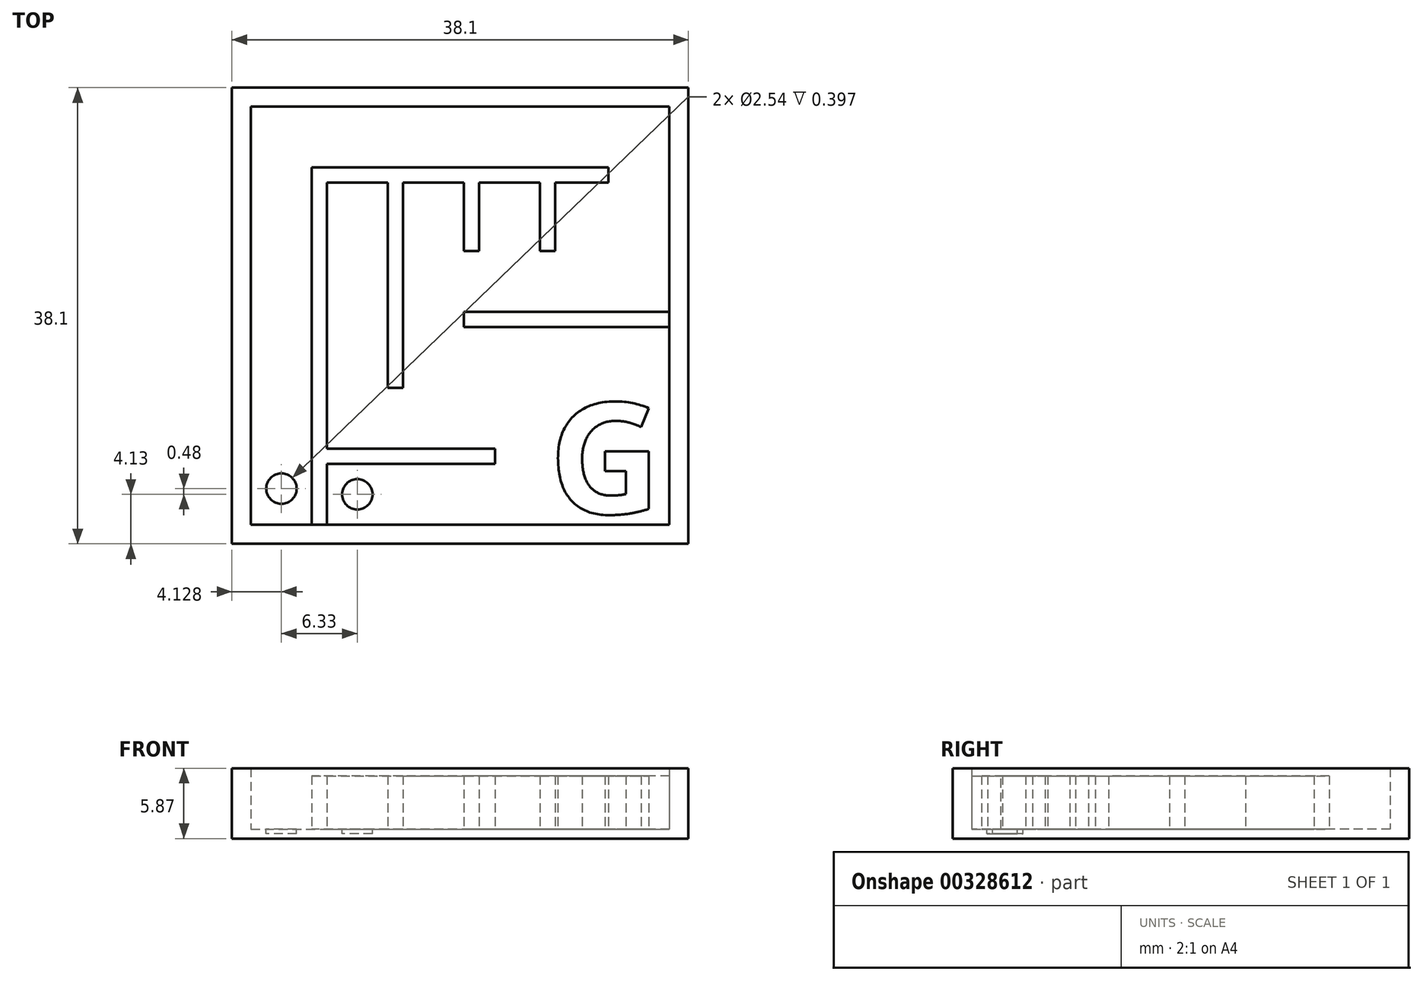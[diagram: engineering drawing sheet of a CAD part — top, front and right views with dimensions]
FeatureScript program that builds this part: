
annotation { "Feature Type Name" : "Feature", "Feature Type Description" : "" }
export const myFeature = defineFeature(function(context is Context, id is Id, definition is map)
    precondition{}
    {
        {
            var Q0;
            Q0=qCreatedBy(makeId("Top.planeOp"),FACE);
            var sketch = newSketch(context, id + "F0", { "sketchPlane" : qUnion([Q0])});
            skLineSegment(sketch, "E0.bottom", {"start": v(-19.76, 15.68) * mm, "end": v(18.34, 15.68) * mm});
            skLineSegment(sketch, "E0.top", {"start": v(-19.76, -22.42) * mm, "end": v(18.34, -22.42) * mm});
            skLineSegment(sketch, "E0.left", {"start": v(-19.76, 15.68) * mm, "end": v(-19.76, -22.42) * mm});
            skLineSegment(sketch, "E0.right", {"start": v(18.34, 15.68) * mm, "end": v(18.34, -22.42) * mm});
            skSolve(sketch);
        }
        {
            var Q0;
            Q0 = qSketchRegion(id + "F0", true);
            extrude(context, id + "F1", {"entities" : qUnion([Q0]), "depth" : 0.8 * mm});
        }
        {
            var Q0;
            Q0=makeQuery(id+"F1.opExtrude","CAP_FACE",FACE,{"disambiguationData":[OSD([sQuery(id+"F0.wireOp",EDGE,"E0.bottom"),sQuery(id+"F0.wireOp",EDGE,"E0.top"),sQuery(id+"F0.wireOp",EDGE,"E0.left"),sQuery(id+"F0.wireOp",EDGE,"E0.right")])],"isStart":false});
            var sketch = newSketch(context, id + "F2", { "sketchPlane" : qUnion([Q0])});
            skLineSegment(sketch, "E1.0", {"start": v(-18.17, 14.1) * mm, "end": v(16.75, 14.1) * mm});
            skLineSegment(sketch, "E1.1", {"start": v(-18.17, 14.1) * mm, "end": v(-18.17, -20.83) * mm});
            skLineSegment(sketch, "E1.2", {"start": v(-18.17, -20.83) * mm, "end": v(16.75, -20.83) * mm});
            skLineSegment(sketch, "E1.3", {"start": v(16.75, 14.1) * mm, "end": v(16.75, -20.83) * mm});
            skSolve(sketch);
        }
        {
            var Q0;
            Q0=makeQuery(id+"F2.imprint","IMPRINT",FACE,{"disambiguationData":[TD([[makeQuery(id+"F2.imprint","IMPRINT",EDGE,{"derivedFrom":sQuery(id+"F2.wireOp",EDGE,"E1.0")}),1.0]])]});
            extrude(context, id + "F3", {"entities" : qUnion([Q0]), "operationType" : NewBodyOperationType.ADD, "depth" : 5.08 * mm});
        }
        {
            var Q0;
            Q0=makeQuery(id+"F1.opExtrude","CAP_FACE",FACE,{"disambiguationData":[OSD([sQuery(id+"F0.wireOp",EDGE,"E0.bottom"),sQuery(id+"F0.wireOp",EDGE,"E0.top"),sQuery(id+"F0.wireOp",EDGE,"E0.left"),sQuery(id+"F0.wireOp",EDGE,"E0.right")])],"isStart":false});
            var sketch = newSketch(context, id + "F4", { "sketchPlane" : qUnion([Q0])});
            skLineSegment(sketch, "E2.bottom", {"start": v(-11.82, -20.83) * mm, "end": v(-13.1, -20.83) * mm});
            skLineSegment(sketch, "E2.top", {"start": v(-11.82, 9.02) * mm, "end": v(-13.1, 9.02) * mm});
            skLineSegment(sketch, "E2.left", {"start": v(-11.82, -20.83) * mm, "end": v(-11.82, 9.02) * mm});
            skLineSegment(sketch, "E2.right", {"start": v(-13.1, -20.83) * mm, "end": v(-13.1, 9.02) * mm});
            skLineSegment(sketch, "E3.bottom", {"start": v(-11.82, 9.02) * mm, "end": v(11.67, 9.02) * mm});
            skLineSegment(sketch, "E3.top", {"start": v(-11.82, 7.75) * mm, "end": v(11.67, 7.75) * mm});
            skLineSegment(sketch, "E3.left", {"start": v(-11.82, 9.02) * mm, "end": v(-11.82, 7.75) * mm});
            skLineSegment(sketch, "E3.right", {"start": v(11.67, 9.02) * mm, "end": v(11.67, 7.75) * mm});
            skLineSegment(sketch, "E4.bottom", {"start": v(-5.47, 7.75) * mm, "end": v(-6.74, 7.75) * mm});
            skLineSegment(sketch, "E4.top", {"start": v(-5.47, -9.4) * mm, "end": v(-6.74, -9.4) * mm});
            skLineSegment(sketch, "E4.left", {"start": v(-5.47, 7.75) * mm, "end": v(-5.47, -9.4) * mm});
            skLineSegment(sketch, "E4.right", {"start": v(-6.74, 7.75) * mm, "end": v(-6.74, -9.4) * mm});
            skLineSegment(sketch, "E5.bottom", {"start": v(16.75, -3.05) * mm, "end": v(-0.4, -3.05) * mm});
            skLineSegment(sketch, "E5.top", {"start": v(16.75, -4.32) * mm, "end": v(-0.4, -4.32) * mm});
            skLineSegment(sketch, "E5.left", {"start": v(16.75, -3.05) * mm, "end": v(16.75, -4.32) * mm});
            skLineSegment(sketch, "E5.right", {"start": v(-0.4, -3.05) * mm, "end": v(-0.4, -4.32) * mm});
            skLineSegment(sketch, "E6.bottom", {"start": v(5.96, 7.75) * mm, "end": v(7.23, 7.75) * mm});
            skLineSegment(sketch, "E6.top", {"start": v(5.96, 2.03) * mm, "end": v(7.23, 2.03) * mm});
            skLineSegment(sketch, "E6.left", {"start": v(5.96, 7.75) * mm, "end": v(5.96, 2.03) * mm});
            skLineSegment(sketch, "E6.right", {"start": v(7.23, 7.75) * mm, "end": v(7.23, 2.03) * mm});
            skLineSegment(sketch, "E7.bottom", {"start": v(-0.4, 7.75) * mm, "end": v(0.88, 7.75) * mm});
            skLineSegment(sketch, "E7.top", {"start": v(-0.4, 2.03) * mm, "end": v(0.88, 2.03) * mm});
            skLineSegment(sketch, "E7.left", {"start": v(-0.4, 7.75) * mm, "end": v(-0.4, 2.03) * mm});
            skLineSegment(sketch, "E7.right", {"start": v(0.88, 7.75) * mm, "end": v(0.88, 2.03) * mm});
            skLineSegment(sketch, "E8.bottom", {"start": v(15.48, -20.83) * mm, "end": v(16.75, -20.83) * mm});
            skLineSegment(sketch, "E9.bottom", {"start": v(10.4, -20.83) * mm, "end": v(9.13, -20.83) * mm});
            skLineSegment(sketch, "E10.bottom", {"start": v(-11.82, -14.48) * mm, "end": v(2.18, -14.48) * mm});
            skLineSegment(sketch, "E10.top", {"start": v(-11.82, -15.75) * mm, "end": v(2.18, -15.75) * mm});
            skLineSegment(sketch, "E10.left", {"start": v(-11.82, -14.48) * mm, "end": v(-11.82, -15.75) * mm});
            skLineSegment(sketch, "E11", {"start": v(-18.17, -20.83) * mm, "end": v(-13.1, -20.83) * mm});
            skPoint(sketch, "E12.centerSnap0", {"position": v(-15.63, -20.83) * mm});
            skLineSegment(sketch, "E13", {"start": v(2.18, -14.48) * mm, "end": v(2.18, -15.75) * mm});
            skSolve(sketch);
        }
        {
            var Q0;
            Q0 = qSketchRegion(id + "F4", true);
            extrude(context, id + "F5", {"entities" : qUnion([Q0]), "operationType" : NewBodyOperationType.ADD, "depth" : 4.44 * mm});
        }
        {
            var Q0;
            Q0=makeQuery(id+"F1.opExtrude","CAP_FACE",FACE,{"disambiguationData":[OSD([sQuery(id+"F0.wireOp",EDGE,"E0.bottom"),sQuery(id+"F0.wireOp",EDGE,"E0.top"),sQuery(id+"F0.wireOp",EDGE,"E0.left"),sQuery(id+"F0.wireOp",EDGE,"E0.right")])],"isStart":false});
            var sketch = newSketch(context, id + "F6", { "sketchPlane" : qUnion([Q0])});
            skLineSegment(sketch, "E14", {"start": v(-18.17, -20.83) * mm, "end": v(-13.1, -20.83) * mm});
            skCircle(sketch, "E15", {"center": v(-15.63, -17.81) * mm, "radius": 1.27 * mm});
            skPoint(sketch, "E15.centerSnap0", {"position": v(-15.63, -20.83) * mm});
            skLineSegment(sketch, "E16", {"start": v(-11.82, -20.83) * mm, "end": v(-11.82, -20.83) * mm});
            skLineSegment(sketch, "E17", {"start": v(-11.82, -15.75) * mm, "end": v(-11.82, -20.83) * mm});
            skCircle(sketch, "E18", {"center": v(-9.3, -18.29) * mm, "radius": 1.27 * mm});
            skPoint(sketch, "E18.centerSnap0", {"position": v(-11.82, -18.29) * mm});
            skSolve(sketch);
        }
        {
            var Q0;
            Q0 = qSketchRegion(id + "F6", true);
            extrude(context, id + "F7", {"entities" : qUnion([Q0]), "operationType" : NewBodyOperationType.REMOVE, "oppositeDirection" : true, "depth" : 0.4 * mm});
        }
        {
            var Q0;
            Q0=makeQuery(id+"F1.opExtrude","CAP_FACE",FACE,{"disambiguationData":[OSD([sQuery(id+"F0.wireOp",EDGE,"E0.bottom"),sQuery(id+"F0.wireOp",EDGE,"E0.top"),sQuery(id+"F0.wireOp",EDGE,"E0.left"),sQuery(id+"F0.wireOp",EDGE,"E0.right")])],"isStart":false});
            var sketch = newSketch(context, id + "F8", { "sketchPlane" : qUnion([Q0])});
            skText(sketch, "E19", { "text": "G\n", "fontName": "OpenSans-Bold.ttf"});
            const initialGuessF8  = {"E19": [0.0067, -0.0199, 1, 0, 0.00932]};
            skSetInitialGuess(sketch, initialGuessF8);
            skSolve(sketch);
        }
        {
            var Q0;
            Q0 = qSketchRegion(id + "F8", true);
            extrude(context, id + "F9", {"entities" : qUnion([Q0]), "operationType" : NewBodyOperationType.ADD, "depth" : 4.44 * mm});
        }
    });
